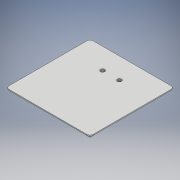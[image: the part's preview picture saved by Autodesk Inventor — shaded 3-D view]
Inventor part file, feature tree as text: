
AUTODESK INVENTOR PART (.ipt)
format: ipt  version: 2017 (Build 210142000, 142)  size: 252,416 bytes
history: native  units: mm
features: reference x4, sketch x2, extrude x1, fillet x1, hole x1, chamfer x1
ambient origin geometry x8: Origin, YZ Plane, XZ Plane, XY Plane, X Axis, Y Axis, Z Axis, Center Point
bodies: Solid1 (feature_tree)
feature tree (10):
  extrude  "Extrusion1"  Depth=80.0mm
  fillet  "Fillet1"  Radius=20.0mm
  hole  "Hole1"  [1 undecoded]
  chamfer  "Chamfer1"  Distance=3.0mm Angle=45.0deg
  sketch  "Sketch1"  dims[d0=80.0mm d1=80.0mm d2=20.0mm]
  reference  "Reference1"
  reference  "Reference2"
  sketch  "Sketch2"  dims[d3=4.0mm d4=0.0mm d5=3.0mm d6=2.1mm d7=6.0mm d8=4.0mm d9=2.0mm d10=90.0deg d11=8.0mm d12=20.594885mm d13=3.0mm d14=2.0mm d15=45.0deg]
  reference  "Reference3"
  reference  "Reference4"
note: 1 required parameter value undecoded (feature->parameter linkage not recoverable at this tier; creation-order binding heuristic only, values carry confidence <= 0.55)
